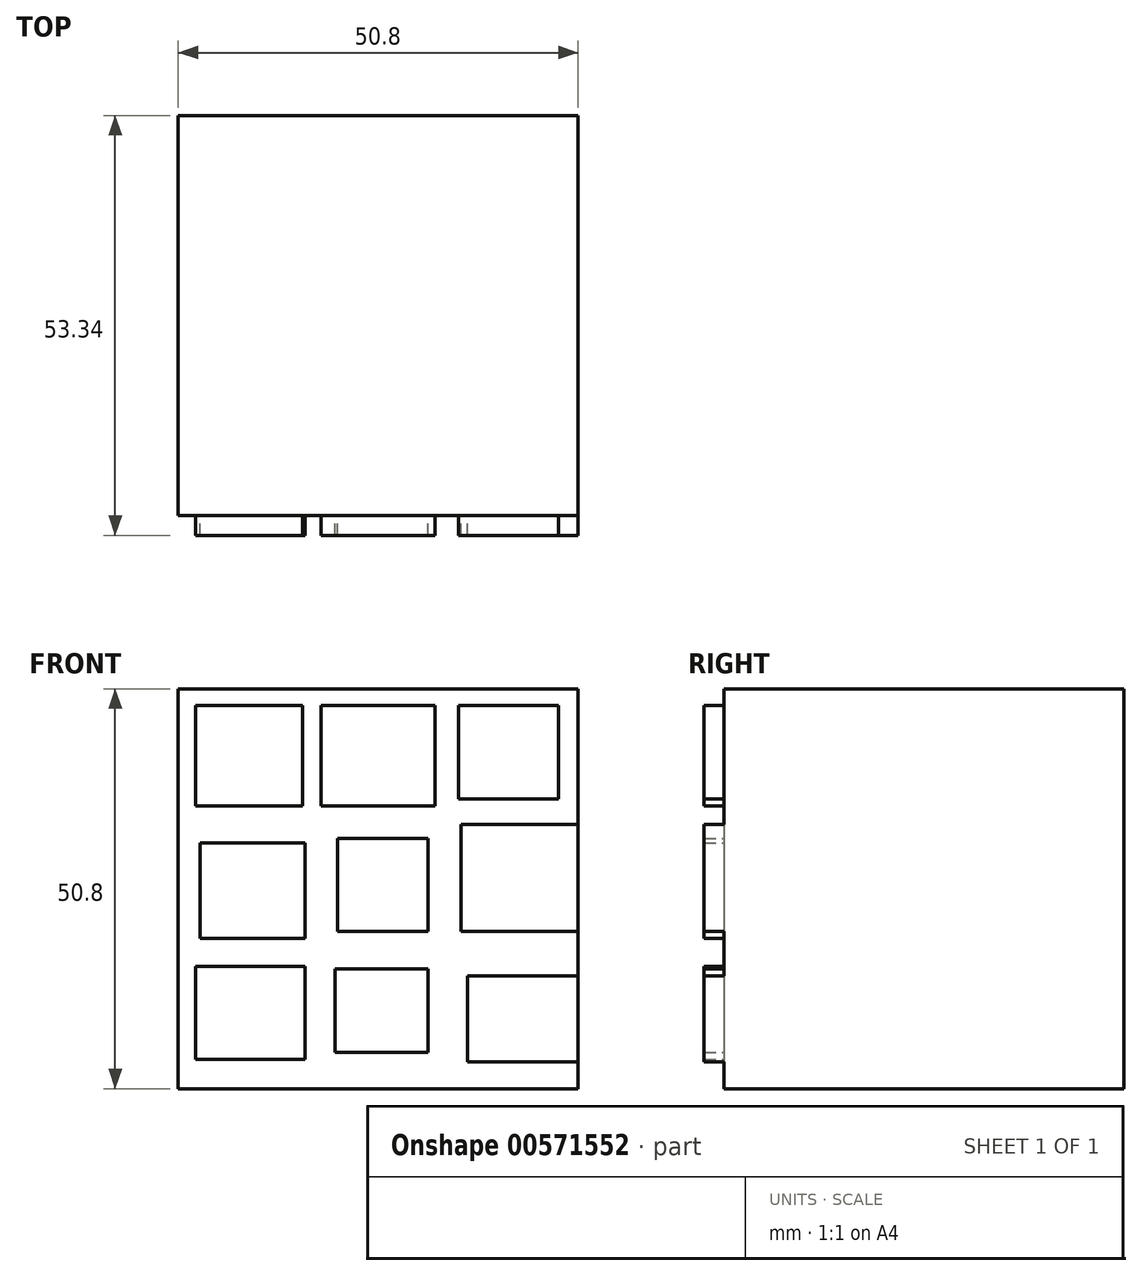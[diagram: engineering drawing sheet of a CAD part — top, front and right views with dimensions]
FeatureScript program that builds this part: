
annotation { "Feature Type Name" : "Feature", "Feature Type Description" : "" }
export const myFeature = defineFeature(function(context is Context, id is Id, definition is map)
    precondition{}
    {
        {
            var Q0;
            Q0=qCreatedBy(makeId("Top.planeOp"),FACE);
            var sketch = newSketch(context, id + "F0", { "sketchPlane" : qUnion([Q0])});
            skLineSegment(sketch, "E0.bottom", {"start": v(25.4, -25.4) * mm, "end": v(-25.4, -25.4) * mm});
            skLineSegment(sketch, "E0.top", {"start": v(25.4, 25.4) * mm, "end": v(-25.4, 25.4) * mm});
            skLineSegment(sketch, "E0.left", {"start": v(25.4, -25.4) * mm, "end": v(25.4, 25.4) * mm});
            skLineSegment(sketch, "E0.right", {"start": v(-25.4, -25.4) * mm, "end": v(-25.4, 25.4) * mm});
            skPoint(sketch, "E0.middle", {"position": v(0, 0) * mm});
            skSolve(sketch);
        }
        {
            var Q0;
            Q0 = qSketchRegion(id + "F0", true);
            extrude(context, id + "F1", {"entities" : qUnion([Q0]), "depth" : 50.8 * mm, "offsetDistance" : 25.4 * mm});
        }
        {
            var Q0;
            Q0=makeQuery(id+"F1.opExtrude","SWEPT_FACE",FACE,{"disambiguationData":[OSD([sQuery(id+"F0.wireOp",EDGE,"E0.bottom")])]});
            var sketch = newSketch(context, id + "F2", { "sketchPlane" : qUnion([Q0])});
            skLineSegment(sketch, "E1.bottom", {"start": v(-23.22, 48.66) * mm, "end": v(-9.61, 48.66) * mm});
            skLineSegment(sketch, "E1.top", {"start": v(-23.22, 35.94) * mm, "end": v(-9.61, 35.94) * mm});
            skLineSegment(sketch, "E1.left", {"start": v(-23.22, 48.66) * mm, "end": v(-23.22, 35.94) * mm});
            skLineSegment(sketch, "E1.right", {"start": v(-9.61, 48.66) * mm, "end": v(-9.61, 35.94) * mm});
            skLineSegment(sketch, "E2.bottom", {"start": v(-22.63, 31.2) * mm, "end": v(-9.32, 31.2) * mm});
            skLineSegment(sketch, "E2.top", {"start": v(-22.63, 19.08) * mm, "end": v(-9.32, 19.08) * mm});
            skLineSegment(sketch, "E2.left", {"start": v(-22.63, 31.2) * mm, "end": v(-22.63, 19.08) * mm});
            skLineSegment(sketch, "E2.right", {"start": v(-9.32, 31.2) * mm, "end": v(-9.32, 19.08) * mm});
            skLineSegment(sketch, "E3.bottom", {"start": v(-7.25, 48.66) * mm, "end": v(7.25, 48.66) * mm});
            skLineSegment(sketch, "E3.top", {"start": v(-7.25, 35.94) * mm, "end": v(7.25, 35.94) * mm});
            skLineSegment(sketch, "E3.left", {"start": v(-7.25, 48.66) * mm, "end": v(-7.25, 35.94) * mm});
            skLineSegment(sketch, "E3.right", {"start": v(7.25, 48.66) * mm, "end": v(7.25, 35.94) * mm});
            skLineSegment(sketch, "E4.bottom", {"start": v(10.2, 48.66) * mm, "end": v(22.92, 48.66) * mm});
            skLineSegment(sketch, "E4.top", {"start": v(10.2, 36.83) * mm, "end": v(22.92, 36.83) * mm});
            skLineSegment(sketch, "E4.left", {"start": v(10.2, 48.66) * mm, "end": v(10.2, 36.83) * mm});
            skLineSegment(sketch, "E4.right", {"start": v(22.92, 48.66) * mm, "end": v(22.92, 36.83) * mm});
            skLineSegment(sketch, "E5.bottom", {"start": v(10.5, 33.57) * mm, "end": v(25.4, 33.57) * mm});
            skLineSegment(sketch, "E5.top", {"start": v(10.5, 19.97) * mm, "end": v(25.4, 19.97) * mm});
            skLineSegment(sketch, "E5.left", {"start": v(10.5, 33.57) * mm, "end": v(10.5, 19.97) * mm});
            skLineSegment(sketch, "E5.right", {"start": v(25.4, 33.57) * mm, "end": v(25.4, 19.97) * mm});
            skLineSegment(sketch, "E6.bottom", {"start": v(-5.18, 31.8) * mm, "end": v(6.36, 31.8) * mm});
            skLineSegment(sketch, "E6.top", {"start": v(-5.18, 19.97) * mm, "end": v(6.36, 19.97) * mm});
            skLineSegment(sketch, "E6.left", {"start": v(-5.18, 31.8) * mm, "end": v(-5.18, 19.97) * mm});
            skLineSegment(sketch, "E6.right", {"start": v(6.36, 31.8) * mm, "end": v(6.36, 19.97) * mm});
            skLineSegment(sketch, "E7.bottom", {"start": v(-23.22, 15.53) * mm, "end": v(-9.32, 15.53) * mm});
            skLineSegment(sketch, "E7.top", {"start": v(-23.22, 3.7) * mm, "end": v(-9.32, 3.7) * mm});
            skLineSegment(sketch, "E7.left", {"start": v(-23.22, 15.53) * mm, "end": v(-23.22, 3.7) * mm});
            skLineSegment(sketch, "E7.right", {"start": v(-9.32, 15.53) * mm, "end": v(-9.32, 3.7) * mm});
            skLineSegment(sketch, "E8.bottom", {"start": v(-5.47, 15.23) * mm, "end": v(6.36, 15.23) * mm});
            skLineSegment(sketch, "E8.top", {"start": v(-5.47, 4.58) * mm, "end": v(6.36, 4.58) * mm});
            skLineSegment(sketch, "E8.left", {"start": v(-5.47, 15.23) * mm, "end": v(-5.47, 4.58) * mm});
            skLineSegment(sketch, "E8.right", {"start": v(6.36, 15.23) * mm, "end": v(6.36, 4.58) * mm});
            skLineSegment(sketch, "E9.bottom", {"start": v(11.38, 14.34) * mm, "end": v(25.4, 14.34) * mm});
            skLineSegment(sketch, "E9.top", {"start": v(11.38, 3.4) * mm, "end": v(25.4, 3.4) * mm});
            skLineSegment(sketch, "E9.left", {"start": v(11.38, 14.34) * mm, "end": v(11.38, 3.4) * mm});
            skLineSegment(sketch, "E9.right", {"start": v(25.4, 14.34) * mm, "end": v(25.4, 3.4) * mm});
            skSolve(sketch);
        }
        {
            var Q0;
            Q0 = qSketchRegion(id + "F2", true);
            extrude(context, id + "F3", {"entities" : qUnion([Q0]), "operationType" : NewBodyOperationType.ADD, "depth" : 2.54 * mm, "offsetDistance" : 25.4 * mm});
        }
    });
